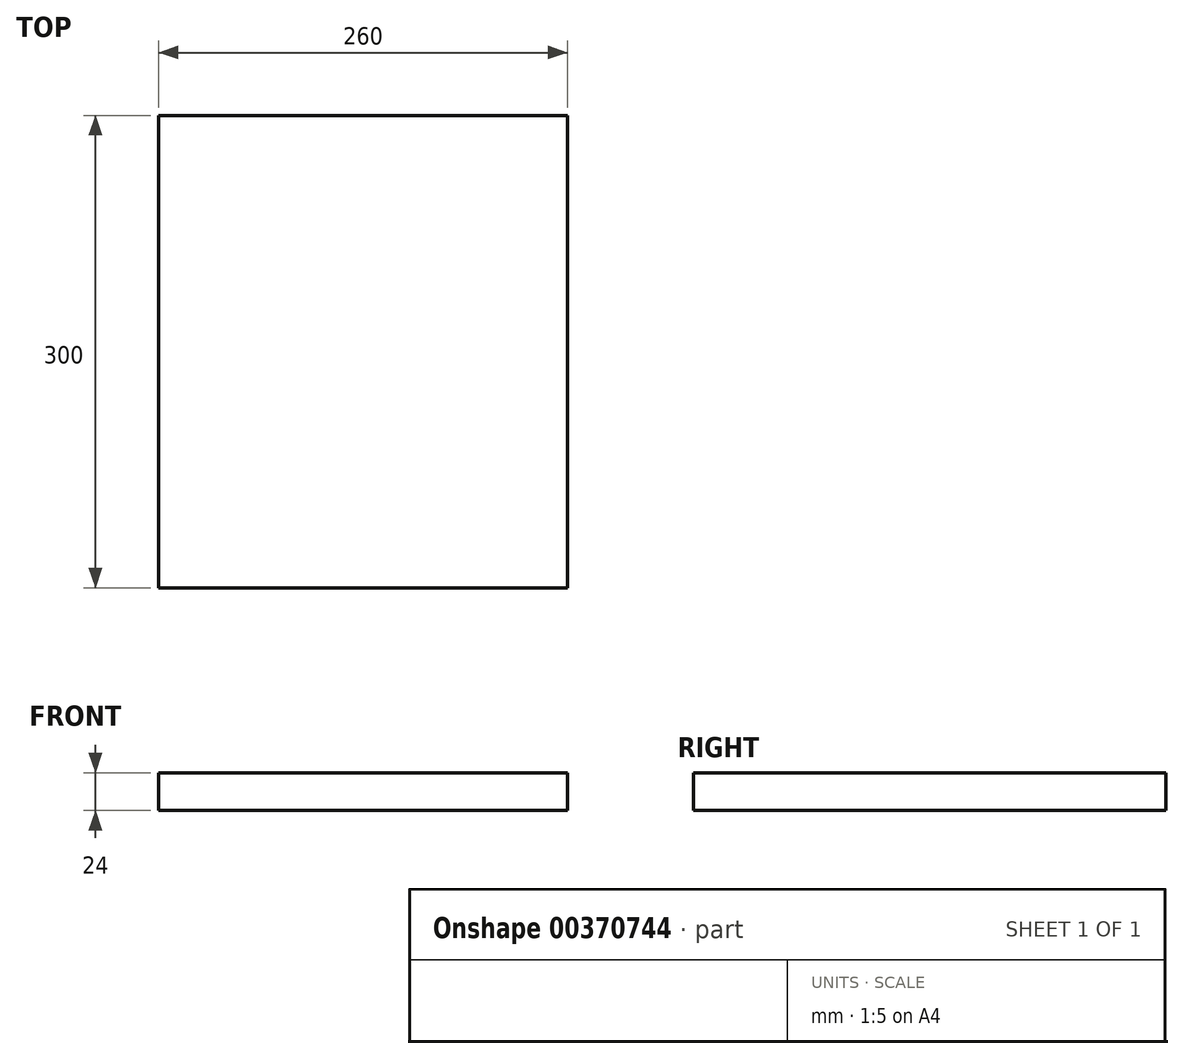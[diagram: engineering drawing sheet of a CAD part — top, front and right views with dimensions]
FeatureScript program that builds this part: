
annotation { "Feature Type Name" : "Feature", "Feature Type Description" : "" }
export const myFeature = defineFeature(function(context is Context, id is Id, definition is map)
    precondition{}
    {
        {
            var Q0;
            Q0=qCreatedBy(makeId("Front.planeOp"),FACE);
            var sketch = newSketch(context, id + "F0", { "sketchPlane" : qUnion([Q0])});
            skLineSegment(sketch, "E0.bottom", {"start": v(130, 12) * mm, "end": v(-130, 12) * mm});
            skLineSegment(sketch, "E0.top", {"start": v(130, -12) * mm, "end": v(-130, -12) * mm});
            skLineSegment(sketch, "E0.left", {"start": v(130, 12) * mm, "end": v(130, -12) * mm});
            skLineSegment(sketch, "E0.right", {"start": v(-130, 12) * mm, "end": v(-130, -12) * mm});
            skPoint(sketch, "E0.middle", {"position": v(0, 0) * mm});
            skSolve(sketch);
        }
        {
            var Q0;
            Q0 = qSketchRegion(id + "F0", true);
            extrude(context, id + "F1", {"entities" : qUnion([Q0]), "oppositeDirection" : true, "depth" : 150 * mm, "hasSecondDirection" : true, "secondDirectionOppositeDirection" : false, "secondDirectionDepth" : 150 * mm});
        }
    });
